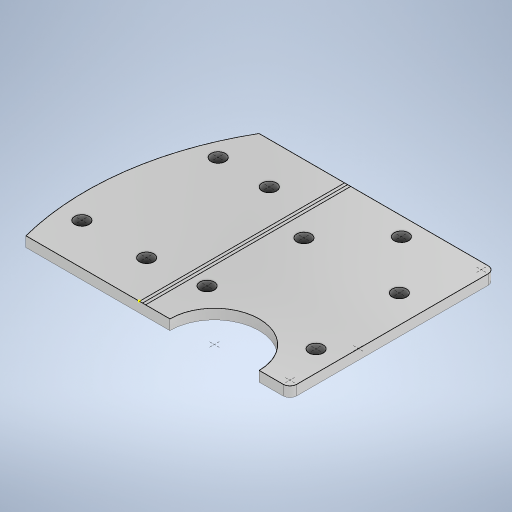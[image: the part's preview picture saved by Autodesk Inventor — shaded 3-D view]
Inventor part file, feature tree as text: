
AUTODESK INVENTOR PART (.ipt)
format: ipt  version: 2024.2 (Build 282272000, 272)  size: 254,976 bytes
history: native  units: in
note: dims shown in document units (in); Inventor stores cm internally (conversion verified against a paired STEP export)
features: sketch x1, extrude x1
ambient origin geometry x8: Origin, YZ Plane, XZ Plane, XY Plane, X Axis, Y Axis, Z Axis, Center Point
bodies: Solid1 (feature_tree)
feature tree (2):
  sketch  "Sketch1"  dims[d0=0.0591in d1=0.0in]
  extrude  "Extrusion1"  [1 undecoded]
note: 1 required parameter value undecoded (feature->parameter linkage not recoverable at this tier; creation-order binding heuristic only, values carry confidence <= 0.55)
